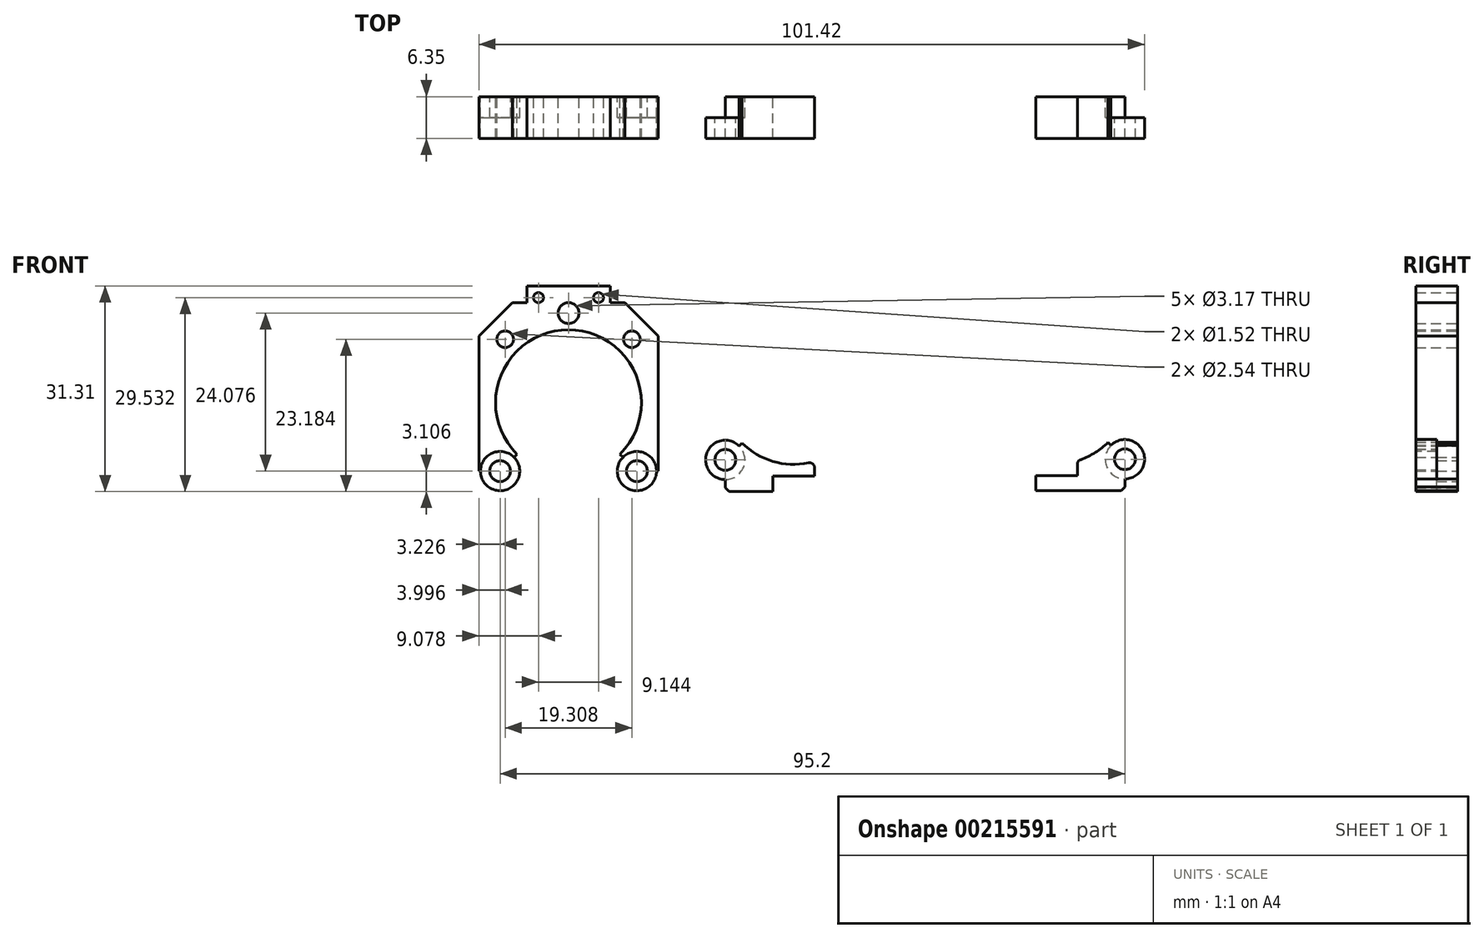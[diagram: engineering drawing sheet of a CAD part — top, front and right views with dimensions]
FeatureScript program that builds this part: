
annotation { "Feature Type Name" : "Feature", "Feature Type Description" : "" }
export const myFeature = defineFeature(function(context is Context, id is Id, definition is map)
    precondition{}
    {
        {
            var Q0;
            Q0=qCreatedBy(makeId("Front.planeOp"),FACE);
            var sketch = newSketch(context, id + "F0", { "sketchPlane" : qUnion([Q0])});
            skCircle(sketch, "E0", {"center": v(0, 0) * mm, "radius": 11.11 * mm});
            skCircle(sketch, "E1", {"center": v(0, 0) * mm, "radius": 13.65 * mm, "construction": true});
            skLineSegment(sketch, "E2.bottom", {"start": v(-13.65, 15.24) * mm, "end": v(-6.35, 15.24) * mm});
            skLineSegment(sketch, "E2.top", {"start": v(-13.65, -15.24) * mm, "end": v(13.65, -15.24) * mm});
            skLineSegment(sketch, "E2.left", {"start": v(-13.65, 15.24) * mm, "end": v(-13.65, -15.24) * mm});
            skLineSegment(sketch, "E2.right", {"start": v(13.65, 15.24) * mm, "end": v(13.65, -15.24) * mm});
            skLineSegment(sketch, "E3", {"start": v(0, 18.7) * mm, "end": v(0, -21.84) * mm, "construction": true});
            skLineSegment(sketch, "E4", {"start": v(-19.31, 0) * mm, "end": v(20.7, 0) * mm, "construction": true});
            skLineSegment(sketch, "E5", {"start": v(0, 0) * mm, "end": v(-18.22, -18.22) * mm, "construction": true});
            skLineSegment(sketch, "E6", {"start": v(0, 0) * mm, "end": v(18.5, -18.5) * mm, "construction": true});
            skLineSegment(sketch, "E7", {"start": v(-8.57, 15.24) * mm, "end": v(-13.65, 10.16) * mm});
            skLineSegment(sketch, "E8", {"start": v(13.65, 10.16) * mm, "end": v(8.57, 15.24) * mm});
            skLineSegment(sketch, "E9.top", {"start": v(-6.35, 17.78) * mm, "end": v(6.35, 17.78) * mm});
            skLineSegment(sketch, "E9.left", {"start": v(-6.35, 15.24) * mm, "end": v(-6.35, 17.78) * mm});
            skLineSegment(sketch, "E9.right", {"start": v(6.35, 15.24) * mm, "end": v(6.35, 17.78) * mm});
            skLineSegment(sketch, "E10", {"start": v(-13.65, -11.43) * mm, "end": v(-9.84, -15.24) * mm});
            skLineSegment(sketch, "E11", {"start": v(13.65, -11.43) * mm, "end": v(9.84, -15.24) * mm});
            skArc(sketch, "E12", {"start": v(-14.74, 0) * mm, "mid": v(0, -14.74) * mm, "end": v(14.74, 0) * mm, "construction": true});
            skCircle(sketch, "E13", {"center": v(-10.42, -10.42) * mm, "radius": 1.59 * mm});
            skCircle(sketch, "E14", {"center": v(10.42, -10.42) * mm, "radius": 1.59 * mm});
            skCircle(sketch, "E15", {"center": v(-10.42, -10.42) * mm, "radius": 3 * mm});
            skCircle(sketch, "E16", {"center": v(10.42, -10.42) * mm, "radius": 3 * mm});
            skLineSegment(sketch, "E17", {"start": v(-8.3, -8.3) * mm, "end": v(-7.86, -7.86) * mm});
            skLineSegment(sketch, "E18", {"start": v(8.3, -8.3) * mm, "end": v(7.86, -7.86) * mm});
            skLineSegment(sketch, "E19.trimOffspring", {"start": v(6.35, 15.24) * mm, "end": v(13.65, 15.24) * mm});
            skLineSegment(sketch, "E20", {"start": v(-5.16, 16) * mm, "end": v(5.36, 16) * mm, "construction": true});
            skCircle(sketch, "E21", {"center": v(-4.57, 16) * mm, "radius": 0.76 * mm});
            skCircle(sketch, "E22", {"center": v(4.57, 16) * mm, "radius": 0.76 * mm});
            skLineSegment(sketch, "E23", {"start": v(0, 0) * mm, "end": v(-11.22, 11.22) * mm, "construction": true});
            skLineSegment(sketch, "E24", {"start": v(0, 0) * mm, "end": v(10.66, 10.66) * mm, "construction": true});
            skCircle(sketch, "E25", {"center": v(-9.65, 9.65) * mm, "radius": 1.27 * mm});
            skCircle(sketch, "E26", {"center": v(9.65, 9.65) * mm, "radius": 1.27 * mm});
            skCircle(sketch, "E27", {"center": v(0, 13.65) * mm, "radius": 1.59 * mm});
            skLineSegment(sketch, "E28", {"start": v(-3.17, -15.24) * mm, "end": v(-3.17, -12.92) * mm});
            skLineSegment(sketch, "E29", {"start": v(-3.17, -12.92) * mm, "end": v(3.18, -12.92) * mm});
            skLineSegment(sketch, "E30", {"start": v(3.18, -12.92) * mm, "end": v(3.18, -10.65) * mm});
            skLineSegment(sketch, "E31", {"start": v(10.42, -10.42) * mm, "end": v(10.42, -15.24) * mm});
            skLineSegment(sketch, "E32", {"start": v(10.42, -10.42) * mm, "end": v(13.65, -10.42) * mm});
            skLineSegment(sketch, "E33", {"start": v(-10.42, -10.42) * mm, "end": v(-10.42, -15.24) * mm});
            skLineSegment(sketch, "E34", {"start": v(-10.42, -15.24) * mm, "end": v(-10.42, -10.42) * mm});
            skLineSegment(sketch, "E35", {"start": v(-10.42, -10.42) * mm, "end": v(-13.65, -10.42) * mm});
            skSolve(sketch);
        }
        {
            var Q0;
            {var subQ1=sQuery(id+"F0.wireOp",EDGE,"E7");Q0=makeQuery(id+"F0.imprint","IMPRINT",FACE,{"disambiguationData":[TD([[makeQuery(id+"F0.imprint","IMPRINT",EDGE,{"derivedFrom":subQ1}),1.0]])]});}
            var Q1;
            Q1=makeQuery(id+"F0.imprint","IMPRINT",FACE,{"disambiguationData":[TD([[makeQuery(id+"F0.imprint","IMPRINT",EDGE,{"derivedFrom":sQuery(id+"F0.wireOp",EDGE,"E13")}),-1.0]])]});
            var Q2;
            Q2=makeQuery(id+"F0.imprint","IMPRINT",FACE,{"disambiguationData":[TD([[makeQuery(id+"F0.imprint","IMPRINT",EDGE,{"derivedFrom":sQuery(id+"F0.wireOp",EDGE,"E14")}),-1.0]])]});
            var Q3;
            {var subQ0=sQuery(id+"F0.wireOp",EDGE,"E17");Q3=makeQuery(id+"F0.imprint","IMPRINT",FACE,{"disambiguationData":[TD([[makeQuery(id+"F0.imprint","IMPRINT",EDGE,{"derivedFrom":subQ0}),1.0]])]});}
            var Q4;
            {var subQ0=sQuery(id+"F0.wireOp",EDGE,"E18");Q4=makeQuery(id+"F0.imprint","IMPRINT",FACE,{"disambiguationData":[TD([[makeQuery(id+"F0.imprint","IMPRINT",EDGE,{"derivedFrom":subQ0}),-1.0]])]});}
            extrude(context, id + "F1", {"entities" : qUnion([Q0, Q1, Q2, Q3, Q4]), "depth" : 6.35 * mm});
        }
        {
            var Q0;
            Q0=makeQuery(id+"F1.opExtrude","CAP_FACE",FACE,{"disambiguationData":[OSD([sQuery(id+"F0.wireOp",EDGE,"E0"),sQuery(id+"F0.wireOp",EDGE,"E2.bottom"),sQuery(id+"F0.wireOp",EDGE,"E2.left"),sQuery(id+"F0.wireOp",EDGE,"E2.right"),sQuery(id+"F0.wireOp",EDGE,"E7"),sQuery(id+"F0.wireOp",EDGE,"E8"),sQuery(id+"F0.wireOp",EDGE,"E9.top"),sQuery(id+"F0.wireOp",EDGE,"E9.left"),sQuery(id+"F0.wireOp",EDGE,"E9.right"),sQuery(id+"F0.wireOp",EDGE,"E10"),sQuery(id+"F0.wireOp",EDGE,"E11"),sQuery(id+"F0.wireOp",EDGE,"E13"),sQuery(id+"F0.wireOp",EDGE,"E14"),sQuery(id+"F0.wireOp",EDGE,"E15"),sQuery(id+"F0.wireOp",EDGE,"E16"),sQuery(id+"F0.wireOp",EDGE,"E17"),sQuery(id+"F0.wireOp",EDGE,"E18"),sQuery(id+"F0.wireOp",EDGE,"E19.trimOffspring"),sQuery(id+"F0.wireOp",EDGE,"E21"),sQuery(id+"F0.wireOp",EDGE,"E22"),sQuery(id+"F0.wireOp",EDGE,"E25"),sQuery(id+"F0.wireOp",EDGE,"E26"),sQuery(id+"F0.wireOp",EDGE,"E27")])],"isStart":false});
            var sketch = newSketch(context, id + "F2", { "sketchPlane" : qUnion([Q0])});
            skCircle(sketch, "E36", {"center": v(-10.42, -10.42) * mm, "radius": 3 * mm});
            skCircle(sketch, "E37", {"center": v(10.42, -10.42) * mm, "radius": 3 * mm});
            skSolve(sketch);
        }
        {
            var Q0;
            Q0 = qSketchRegion(id + "F2", true);
            extrude(context, id + "F3", {"entities" : qUnion([Q0]), "operationType" : NewBodyOperationType.REMOVE, "oppositeDirection" : true, "depth" : 3.17 * mm});
        }
        {
            var Q0;
            Q0=qCreatedBy(makeId("Front.planeOp"),FACE);
            var sketch = newSketch(context, id + "F4", { "sketchPlane" : qUnion([Q0])});
            skCircle(sketch, "E38", {"center": v(34.32, 1.7) * mm, "radius": 11.11 * mm});
            skCircle(sketch, "E39", {"center": v(34.32, 1.7) * mm, "radius": 13.65 * mm, "construction": true});
            skLineSegment(sketch, "E40.bottom", {"start": v(20.67, 16.95) * mm, "end": v(27.97, 16.95) * mm});
            skLineSegment(sketch, "E40.top", {"start": v(20.67, -13.53) * mm, "end": v(47.97, -13.53) * mm});
            skLineSegment(sketch, "E40.left", {"start": v(20.67, 16.95) * mm, "end": v(20.67, -13.53) * mm});
            skLineSegment(sketch, "E40.right", {"start": v(47.97, 16.95) * mm, "end": v(47.97, -13.53) * mm});
            skLineSegment(sketch, "E41", {"start": v(34.32, 20.4) * mm, "end": v(34.32, -20.14) * mm, "construction": true});
            skLineSegment(sketch, "E42", {"start": v(15, 1.7) * mm, "end": v(55.02, 1.7) * mm, "construction": true});
            skLineSegment(sketch, "E43", {"start": v(34.32, 1.7) * mm, "end": v(16.1, -16.51) * mm, "construction": true});
            skLineSegment(sketch, "E44", {"start": v(34.32, 1.7) * mm, "end": v(52.8, -16.78) * mm, "construction": true});
            skLineSegment(sketch, "E45", {"start": v(25.75, 16.95) * mm, "end": v(20.67, 11.87) * mm});
            skLineSegment(sketch, "E46", {"start": v(47.97, 11.87) * mm, "end": v(42.9, 16.95) * mm});
            skLineSegment(sketch, "E47.top", {"start": v(27.97, 19.49) * mm, "end": v(40.67, 19.49) * mm});
            skLineSegment(sketch, "E47.left", {"start": v(27.97, 16.95) * mm, "end": v(27.97, 19.49) * mm});
            skLineSegment(sketch, "E47.right", {"start": v(40.67, 16.95) * mm, "end": v(40.67, 19.49) * mm});
            skLineSegment(sketch, "E48", {"start": v(20.67, -9.72) * mm, "end": v(24.48, -13.53) * mm});
            skLineSegment(sketch, "E49", {"start": v(47.97, -9.72) * mm, "end": v(44.16, -13.53) * mm});
            skArc(sketch, "E50", {"start": v(19.58, 1.7) * mm, "mid": v(34.32, -13.03) * mm, "end": v(49.06, 1.7) * mm, "construction": true});
            skCircle(sketch, "E51", {"center": v(23.9, -8.72) * mm, "radius": 1.59 * mm});
            skCircle(sketch, "E52", {"center": v(44.74, -8.72) * mm, "radius": 1.59 * mm});
            skCircle(sketch, "E53", {"center": v(23.9, -8.72) * mm, "radius": 3 * mm});
            skCircle(sketch, "E54", {"center": v(44.74, -8.72) * mm, "radius": 3 * mm});
            skLineSegment(sketch, "E55", {"start": v(26.01, -6.6) * mm, "end": v(26.46, -6.15) * mm});
            skLineSegment(sketch, "E56", {"start": v(42.63, -6.6) * mm, "end": v(42.18, -6.15) * mm});
            skLineSegment(sketch, "E57.trimOffspring", {"start": v(40.67, 16.95) * mm, "end": v(47.97, 16.95) * mm});
            skLineSegment(sketch, "E58", {"start": v(29.16, 17.7) * mm, "end": v(39.68, 17.7) * mm, "construction": true});
            skCircle(sketch, "E59", {"center": v(29.75, 17.7) * mm, "radius": 0.76 * mm});
            skCircle(sketch, "E60", {"center": v(38.9, 17.7) * mm, "radius": 0.76 * mm});
            skLineSegment(sketch, "E61", {"start": v(34.32, 1.7) * mm, "end": v(23.1, 12.93) * mm, "construction": true});
            skLineSegment(sketch, "E62", {"start": v(34.32, 1.7) * mm, "end": v(44.98, 12.37) * mm, "construction": true});
            skCircle(sketch, "E63", {"center": v(24.67, 11.36) * mm, "radius": 1.59 * mm});
            skCircle(sketch, "E64", {"center": v(43.97, 11.36) * mm, "radius": 1.59 * mm});
            skCircle(sketch, "E65", {"center": v(34.32, 15.36) * mm, "radius": 1.59 * mm});
            skLineSegment(sketch, "E66", {"start": v(31.14, -13.53) * mm, "end": v(31.14, -11.2) * mm});
            skLineSegment(sketch, "E67", {"start": v(31.14, -11.2) * mm, "end": v(37.5, -11.2) * mm});
            skLineSegment(sketch, "E68", {"start": v(37.5, -11.2) * mm, "end": v(37.5, -8.94) * mm});
            skLineSegment(sketch, "E69", {"start": v(44.74, -8.72) * mm, "end": v(44.74, -13.53) * mm});
            skLineSegment(sketch, "E70", {"start": v(44.74, -8.72) * mm, "end": v(47.97, -8.72) * mm});
            skLineSegment(sketch, "E71", {"start": v(23.9, -8.72) * mm, "end": v(23.9, -13.53) * mm});
            skLineSegment(sketch, "E72", {"start": v(23.9, -13.53) * mm, "end": v(23.9, -8.72) * mm});
            skLineSegment(sketch, "E73", {"start": v(23.9, -8.72) * mm, "end": v(20.67, -8.72) * mm});
            skSolve(sketch);
        }
        {
            var Q0;
            {var subQ2=sQuery(id+"F4.wireOp",EDGE,"E72");var subQ6=sQuery(id+"F4.wireOp",EDGE,"E51");var subQ7=makeQuery(id+"F4.imprint","INTERSECT",VERTEX,{"derivedFrom":[subQ6,subQ2]});Q0=makeQuery(id+"F4.imprint","IMPRINT",FACE,{"disambiguationData":[TD([[makeQuery(id+"F4.imprint","IMPRINT",EDGE,{"disambiguationData":[TD([[subQ7,-1.0]])],"derivedFrom":subQ6}),-1.0]])]});}
            var Q1;
            {var subQ2=sQuery(id+"F4.wireOp",EDGE,"E72");var subQ4=sQuery(id+"F4.wireOp",EDGE,"E51");var subQ5=makeQuery(id+"F4.imprint","INTERSECT",VERTEX,{"derivedFrom":[subQ4,subQ2]});Q1=makeQuery(id+"F4.imprint","IMPRINT",FACE,{"disambiguationData":[TD([[makeQuery(id+"F4.imprint","IMPRINT",EDGE,{"disambiguationData":[TD([[subQ5,1.0]])],"derivedFrom":subQ4}),-1.0]])]});}
            var Q2;
            {var subQ6=sQuery(id+"F4.wireOp",EDGE,"E55");Q2=makeQuery(id+"F4.imprint","IMPRINT",FACE,{"disambiguationData":[TD([[makeQuery(id+"F4.imprint","IMPRINT",EDGE,{"derivedFrom":subQ6}),-1.0]])]});}
            extrude(context, id + "F5", {"entities" : qUnion([Q0, Q1, Q2]), "depth" : 6.35 * mm});
        }
        {
            var Q0;
            Q0=qCreatedBy(makeId("Front.planeOp"),FACE);
            var sketch = newSketch(context, id + "F6", { "sketchPlane" : qUnion([Q0])});
            skCircle(sketch, "E74", {"center": v(74.35, 1.81) * mm, "radius": 11.11 * mm});
            skCircle(sketch, "E75", {"center": v(74.35, 1.81) * mm, "radius": 13.65 * mm, "construction": true});
            skLineSegment(sketch, "E76.bottom", {"start": v(60.7, 17.05) * mm, "end": v(68, 17.05) * mm});
            skLineSegment(sketch, "E76.top", {"start": v(60.7, -13.43) * mm, "end": v(88, -13.43) * mm});
            skLineSegment(sketch, "E76.left", {"start": v(60.7, 17.05) * mm, "end": v(60.7, -13.43) * mm});
            skLineSegment(sketch, "E76.right", {"start": v(88, 17.05) * mm, "end": v(88, -13.43) * mm});
            skLineSegment(sketch, "E77", {"start": v(74.35, 20.5) * mm, "end": v(74.35, -20.03) * mm, "construction": true});
            skLineSegment(sketch, "E78", {"start": v(55.04, 1.81) * mm, "end": v(95.06, 1.81) * mm, "construction": true});
            skLineSegment(sketch, "E79", {"start": v(74.35, 1.81) * mm, "end": v(56.13, -16.4) * mm, "construction": true});
            skLineSegment(sketch, "E80", {"start": v(74.35, 1.81) * mm, "end": v(92.84, -16.68) * mm, "construction": true});
            skLineSegment(sketch, "E81", {"start": v(65.78, 17.05) * mm, "end": v(60.7, 11.97) * mm});
            skLineSegment(sketch, "E82", {"start": v(88, 11.97) * mm, "end": v(82.92, 17.05) * mm});
            skLineSegment(sketch, "E83.top", {"start": v(68, 19.6) * mm, "end": v(80.7, 19.6) * mm});
            skLineSegment(sketch, "E83.left", {"start": v(68, 17.05) * mm, "end": v(68, 19.6) * mm});
            skLineSegment(sketch, "E83.right", {"start": v(80.7, 17.05) * mm, "end": v(80.7, 19.6) * mm});
            skLineSegment(sketch, "E84", {"start": v(60.7, -9.62) * mm, "end": v(64.5, -13.43) * mm});
            skLineSegment(sketch, "E85", {"start": v(88, -9.62) * mm, "end": v(84.2, -13.43) * mm});
            skArc(sketch, "E86", {"start": v(59.61, 1.81) * mm, "mid": v(74.35, -12.93) * mm, "end": v(89.1, 1.81) * mm, "construction": true});
            skCircle(sketch, "E87", {"center": v(63.93, -8.61) * mm, "radius": 1.59 * mm});
            skCircle(sketch, "E88", {"center": v(84.78, -8.61) * mm, "radius": 1.59 * mm});
            skCircle(sketch, "E89", {"center": v(63.93, -8.61) * mm, "radius": 3 * mm});
            skCircle(sketch, "E90", {"center": v(84.78, -8.61) * mm, "radius": 3 * mm});
            skLineSegment(sketch, "E91", {"start": v(66.05, -6.5) * mm, "end": v(66.5, -6.05) * mm});
            skLineSegment(sketch, "E92", {"start": v(82.66, -6.5) * mm, "end": v(82.2, -6.05) * mm});
            skLineSegment(sketch, "E93.trimOffspring", {"start": v(80.7, 17.05) * mm, "end": v(88, 17.05) * mm});
            skLineSegment(sketch, "E94", {"start": v(69.19, 17.81) * mm, "end": v(79.72, 17.81) * mm, "construction": true});
            skCircle(sketch, "E95", {"center": v(69.78, 17.81) * mm, "radius": 0.76 * mm});
            skCircle(sketch, "E96", {"center": v(78.92, 17.81) * mm, "radius": 0.76 * mm});
            skLineSegment(sketch, "E97", {"start": v(74.35, 1.81) * mm, "end": v(63.13, 13.03) * mm, "construction": true});
            skLineSegment(sketch, "E98", {"start": v(74.35, 1.81) * mm, "end": v(85.01, 12.47) * mm, "construction": true});
            skCircle(sketch, "E99", {"center": v(64.7, 11.47) * mm, "radius": 1.59 * mm});
            skCircle(sketch, "E100", {"center": v(84, 11.47) * mm, "radius": 1.59 * mm});
            skCircle(sketch, "E101", {"center": v(74.35, 15.46) * mm, "radius": 1.59 * mm});
            skLineSegment(sketch, "E102", {"start": v(71.18, -13.43) * mm, "end": v(71.18, -11.1) * mm});
            skLineSegment(sketch, "E103", {"start": v(71.18, -11.1) * mm, "end": v(77.53, -11.1) * mm});
            skLineSegment(sketch, "E104", {"start": v(77.53, -11.1) * mm, "end": v(77.53, -8.84) * mm});
            skLineSegment(sketch, "E105", {"start": v(84.78, -8.61) * mm, "end": v(84.78, -13.43) * mm});
            skLineSegment(sketch, "E106", {"start": v(84.78, -8.61) * mm, "end": v(88, -8.61) * mm});
            skLineSegment(sketch, "E107", {"start": v(63.93, -8.61) * mm, "end": v(63.93, -13.43) * mm});
            skLineSegment(sketch, "E108", {"start": v(63.93, -13.43) * mm, "end": v(63.93, -8.61) * mm});
            skLineSegment(sketch, "E109", {"start": v(63.93, -8.61) * mm, "end": v(60.7, -8.61) * mm});
            skSolve(sketch);
        }
        {
            var Q0;
            {var subQ5=sQuery(id+"F6.wireOp",EDGE,"E92");Q0=makeQuery(id+"F6.imprint","IMPRINT",FACE,{"disambiguationData":[TD([[makeQuery(id+"F6.imprint","IMPRINT",EDGE,{"derivedFrom":subQ5}),1.0]])]});}
            var Q1;
            {var subQ2=sQuery(id+"F6.wireOp",EDGE,"E105");var subQ4=sQuery(id+"F6.wireOp",EDGE,"E88");var subQ5=makeQuery(id+"F6.imprint","INTERSECT",VERTEX,{"derivedFrom":[subQ4,subQ2]});Q1=makeQuery(id+"F6.imprint","IMPRINT",FACE,{"disambiguationData":[TD([[makeQuery(id+"F6.imprint","IMPRINT",EDGE,{"disambiguationData":[TD([[subQ5,1.0]])],"derivedFrom":subQ4}),-1.0]])]});}
            var Q2;
            {var subQ2=sQuery(id+"F6.wireOp",EDGE,"E105");var subQ5=sQuery(id+"F6.wireOp",EDGE,"E88");var subQ8=makeQuery(id+"F6.imprint","INTERSECT",VERTEX,{"derivedFrom":[subQ5,subQ2]});Q2=makeQuery(id+"F6.imprint","IMPRINT",FACE,{"disambiguationData":[TD([[makeQuery(id+"F6.imprint","IMPRINT",EDGE,{"disambiguationData":[TD([[subQ8,-1.0]])],"derivedFrom":subQ5}),-1.0]])]});}
            extrude(context, id + "F7", {"entities" : qUnion([Q0, Q1, Q2]), "depth" : 6.35 * mm});
        }
        {
            var Q0;
            Q0=makeQuery(id+"F5.opExtrude","CAP_FACE",FACE,{"disambiguationData":[OSD([sQuery(id+"F4.wireOp",EDGE,"E38"),sQuery(id+"F4.wireOp",EDGE,"E40.top"),sQuery(id+"F4.wireOp",EDGE,"E48"),sQuery(id+"F4.wireOp",EDGE,"E51"),sQuery(id+"F4.wireOp",EDGE,"E53"),sQuery(id+"F4.wireOp",EDGE,"E55"),sQuery(id+"F4.wireOp",EDGE,"E66"),sQuery(id+"F4.wireOp",EDGE,"E67"),sQuery(id+"F4.wireOp",EDGE,"E68"),sQuery(id+"F4.wireOp",EDGE,"E72")])],"isStart":true});
            var sketch = newSketch(context, id + "F8", { "sketchPlane" : qUnion([Q0])});
            skCircle(sketch, "E110", {"center": v(-23.9, -8.72) * mm, "radius": 3 * mm});
            skSolve(sketch);
        }
        {
            var Q0;
            Q0 = qSketchRegion(id + "F8", true);
            extrude(context, id + "F9", {"entities" : qUnion([Q0]), "operationType" : NewBodyOperationType.REMOVE, "oppositeDirection" : true, "depth" : 3.17 * mm});
        }
        {
            var Q0;
            Q0=makeQuery(id+"F7.opExtrude","CAP_FACE",FACE,{"disambiguationData":[OSD([sQuery(id+"F6.wireOp",EDGE,"E74"),sQuery(id+"F6.wireOp",EDGE,"E76.top"),sQuery(id+"F6.wireOp",EDGE,"E85"),sQuery(id+"F6.wireOp",EDGE,"E88"),sQuery(id+"F6.wireOp",EDGE,"E90"),sQuery(id+"F6.wireOp",EDGE,"E92"),sQuery(id+"F6.wireOp",EDGE,"E102"),sQuery(id+"F6.wireOp",EDGE,"E103"),sQuery(id+"F6.wireOp",EDGE,"E104"),sQuery(id+"F6.wireOp",EDGE,"E105")])],"isStart":true});
            var sketch = newSketch(context, id + "F10", { "sketchPlane" : qUnion([Q0])});
            skCircle(sketch, "E111", {"center": v(-84.78, -8.61) * mm, "radius": 3 * mm});
            skSolve(sketch);
        }
        {
            var Q0;
            Q0 = qSketchRegion(id + "F10", true);
            extrude(context, id + "F11", {"entities" : qUnion([Q0]), "operationType" : NewBodyOperationType.REMOVE, "oppositeDirection" : true, "depth" : 3.17 * mm});
        }
        {
            var Q0;
            Q0=makeQuery(id+"F5.opExtrude","SWEPT_EDGE",EDGE,{"disambiguationData":[OSD([sQuery(id+"F4.wireOp",EDGE,"E38"),sQuery(id+"F4.wireOp",EDGE,"E68")])]});
            fillet(context, id + "F12", {"entities" : qUnion([Q0]), "radius" : 0.76 * mm, "tangentPropagation" : true, "allowEdgeOverflow" : false});
        }
        {
            var Q0;
            Q0=makeQuery(id+"F7.opExtrude","SWEPT_EDGE",EDGE,{"disambiguationData":[OSD([sQuery(id+"F6.wireOp",EDGE,"E74"),sQuery(id+"F6.wireOp",EDGE,"E104")])]});
            fillet(context, id + "F13", {"entities" : qUnion([Q0]), "radius" : 0.76 * mm, "tangentPropagation" : true, "allowEdgeOverflow" : false});
        }
    });
